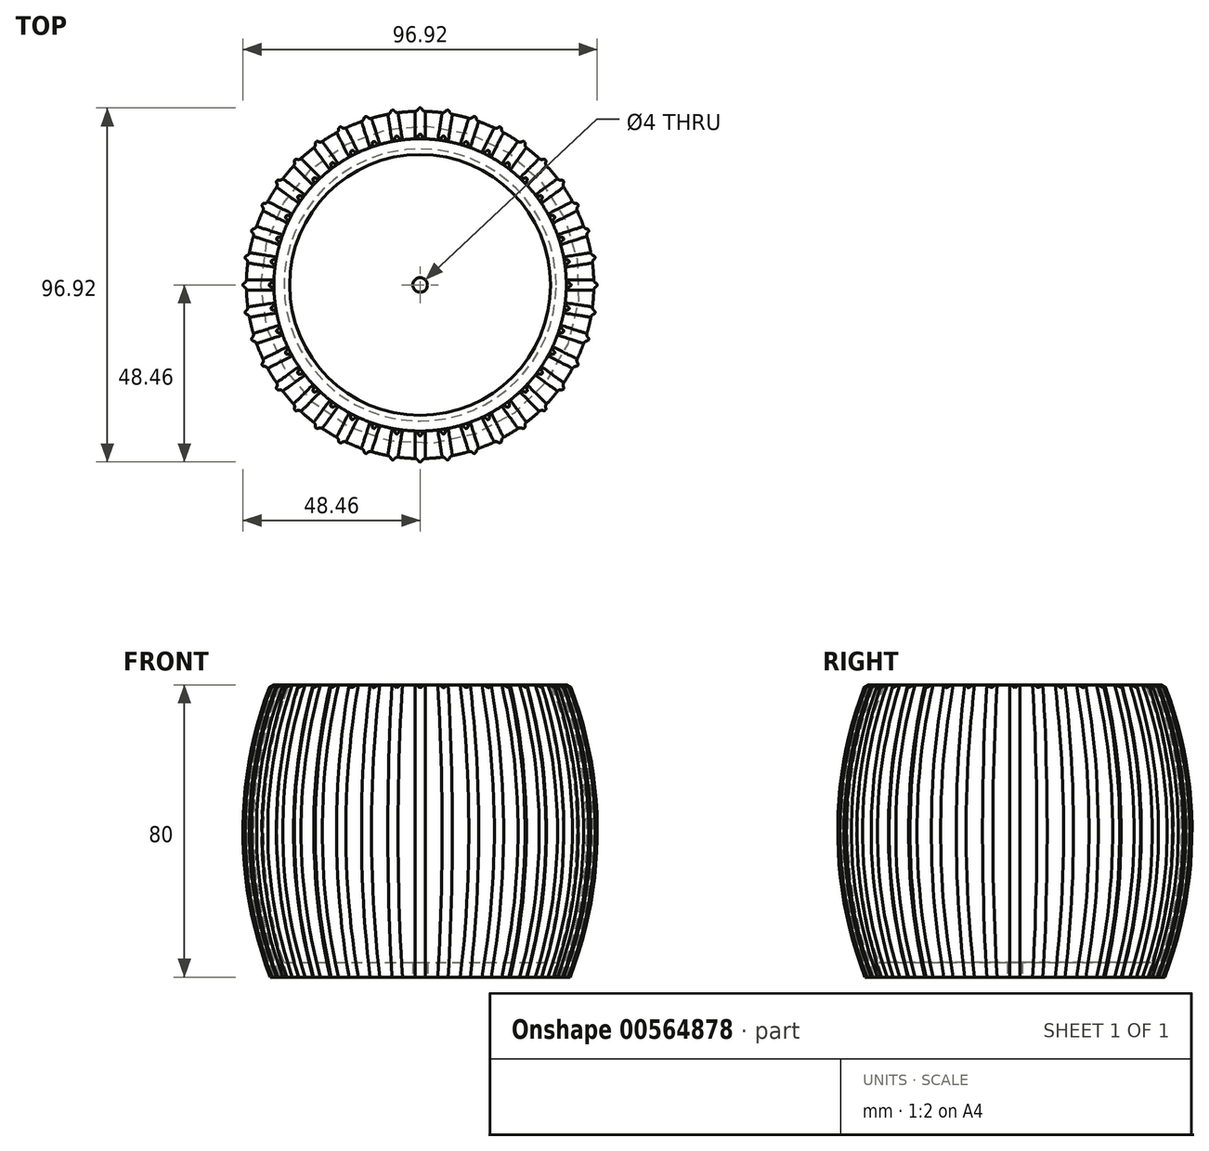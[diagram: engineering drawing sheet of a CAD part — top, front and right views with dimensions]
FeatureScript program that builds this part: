
annotation { "Feature Type Name" : "Feature", "Feature Type Description" : "" }
export const myFeature = defineFeature(function(context is Context, id is Id, definition is map)
    precondition{}
    {
        {
            var Q0;
            Q0=qCreatedBy(makeId("Front.planeOp"),FACE);
            var sketch = newSketch(context, id + "F0", { "sketchPlane" : qUnion([Q0])});
            skLineSegment(sketch, "E0", {"start": v(2, 0) * mm, "end": v(40, 0) * mm});
            skPoint(sketch, "E1", {"position": v(47.53, 40) * mm});
            skArc(sketch, "E2", {"start": v(40, 0) * mm, "mid": v(47.53, 40) * mm, "end": v(40, 80) * mm});
            skArc(sketch, "E3.0", {"start": v(37.23, 4) * mm, "mid": v(43.5, 42.14) * mm, "end": v(35.7, 80) * mm});
            skLineSegment(sketch, "E4", {"start": v(40, 80) * mm, "end": v(35.7, 80) * mm});
            skLineSegment(sketch, "E5", {"start": v(2, 4) * mm, "end": v(37.23, 4) * mm});
            skLineSegment(sketch, "E6", {"start": v(2, 4) * mm, "end": v(2, 0) * mm});
            skLineSegment(sketch, "E7", {"start": v(0, 0) * mm, "end": v(0, 28.98) * mm, "construction": true});
            skSolve(sketch);
        }
        {
            var Q0;
            Q0=makeQuery(id+"F0.imprint","IMPRINT",FACE,{"disambiguationData":[TD([[makeQuery(id+"F0.imprint","IMPRINT",EDGE,{"derivedFrom":sQuery(id+"F0.wireOp",EDGE,"E0")}),1.0]])]});
            var Q1;
            Q1=sQuery(id+"F0.wireOp",EDGE,"E7");
            revolve(context, id + "F1", {"entities" : qUnion([Q0]), "axis" : qUnion([Q1]), "revolveType" : RevolveType.FULL});
        }
        {
            var Q0;
            Q0=qCreatedBy(makeId("Top.planeOp"),FACE);
            var sketch = newSketch(context, id + "F2", { "sketchPlane" : qUnion([Q0])});
            skLineSegment(sketch, "E8", {"start": v(40.47, -0.6) * mm, "end": v(40.75, -0.43) * mm});
            skLineSegment(sketch, "E9", {"start": v(40.75, 0.43) * mm, "end": v(40.47, 0.6) * mm});
            skPoint(sketch, "E10.visualSharp", {"position": v(41.5, 0) * mm});
            skArc(sketch, "E10.filletArc", {"start": v(40.75, -0.43) * mm, "mid": v(41, 0) * mm, "end": v(40.75, 0.43) * mm});
            skPoint(sketch, "E11.center", {"position": v(0, 0) * mm});
            skPoint(sketch, "E12.visualSharp", {"position": v(40, 0.87) * mm});
            skArc(sketch, "E12.filletArc", {"start": v(39.97, 1.42) * mm, "mid": v(40.12, 0.94) * mm, "end": v(40.47, 0.6) * mm});
            skPoint(sketch, "E13.visualSharp", {"position": v(40, -0.87) * mm});
            skArc(sketch, "E13.filletArc", {"start": v(40.47, -0.6) * mm, "mid": v(40.12, -0.94) * mm, "end": v(39.97, -1.42) * mm});
            skArc(sketch, "E14.converted", {"start": v(39.97, 1.42) * mm, "mid": v(40, 0) * mm, "end": v(39.97, -1.42) * mm});
            skSolve(sketch);
        }
        {
            var Q0;
            {var subQ0=sQuery(id+"F2.wireOp",EDGE,"E8");Q0=makeQuery(id+"F2.imprint","IMPRINT",FACE,{"disambiguationData":[TD([[makeQuery(id+"F2.imprint","IMPRINT",EDGE,{"derivedFrom":subQ0}),1.0]])]});}
            var Q1;
            Q1=sQuery(id+"F0.wireOp",EDGE,"E2");
            sweep(context, id + "F3", {"operationType" : NewBodyOperationType.ADD, "profiles" : qUnion([Q0]), "path" : qUnion([Q1])});
        }
        {
            var Q0;
            Q0=makeQuery(id+"F3.opSweep","SWEPT_FACE",FACE,{"disambiguationData":[OSD([sQuery(id+"F0.wireOp",EDGE,"E2"),sQuery(id+"F2.wireOp",EDGE,"E13.filletArc")])]});
            var Q1;
            Q1=makeQuery(id+"F3.opSweep","SWEPT_FACE",FACE,{"disambiguationData":[OSD([sQuery(id+"F0.wireOp",EDGE,"E2"),sQuery(id+"F2.wireOp",EDGE,"E8")])]});
            var Q2;
            Q2=makeQuery(id+"F3.opSweep","SWEPT_FACE",FACE,{"disambiguationData":[OSD([sQuery(id+"F0.wireOp",EDGE,"E2"),sQuery(id+"F2.wireOp",EDGE,"E10.filletArc")])]});
            var Q3;
            Q3=makeQuery(id+"F3.opSweep","SWEPT_FACE",FACE,{"disambiguationData":[OSD([sQuery(id+"F0.wireOp",EDGE,"E2"),sQuery(id+"F2.wireOp",EDGE,"E9")])]});
            var Q4;
            Q4=makeQuery(id+"F3.opSweep","SWEPT_FACE",FACE,{"disambiguationData":[OSD([sQuery(id+"F0.wireOp",EDGE,"E2"),sQuery(id+"F2.wireOp",EDGE,"E12.filletArc")])]});
            var Q5;
            Q5=makeQuery(id+"F3.opSweep","CAP_FACE",FACE,{"disambiguationData":[OSD([sQuery(id+"F0.wireOp",VERTEX,"E2.end"),sQuery(id+"F2.wireOp",EDGE,"E8"),sQuery(id+"F2.wireOp",EDGE,"E9"),sQuery(id+"F2.wireOp",EDGE,"E10.filletArc"),sQuery(id+"F2.wireOp",EDGE,"E12.filletArc"),sQuery(id+"F2.wireOp",EDGE,"E13.filletArc"),sQuery(id+"F2.wireOp",EDGE,"E14.converted")])],"isStart":false});
            var Q6;
            Q6=sQuery(id+"F0.wireOp",EDGE,"E7");
            circularPattern(context, id + "F4", {"patternType" : PatternType.FACE, "faces" : qUnion([Q0, Q1, Q2, Q3, Q4, Q5]), "axis" : qUnion([Q6]), "angle" : 360 * degree, "instanceCount" : 40, "equalSpace" : true});
        }
        {
            var Q0;
            Q0=qCreatedBy(makeId("Front.planeOp"),FACE);
            var sketch = newSketch(context, id + "F5", { "sketchPlane" : qUnion([Q0])});
            skPoint(sketch, "E15.0", {"position": v(40, 80) * mm});
            skLineSegment(sketch, "E16", {"start": v(40, 80) * mm, "end": v(42, 78.85) * mm});
            skLineSegment(sketch, "E17", {"start": v(40, 80) * mm, "end": v(42, 80) * mm, "construction": true});
            skLineSegment(sketch, "E18", {"start": v(42, 81) * mm, "end": v(42, 78.85) * mm});
            skLineSegment(sketch, "E19", {"start": v(40, 80) * mm, "end": v(40, 81) * mm});
            skLineSegment(sketch, "E20", {"start": v(40, 81) * mm, "end": v(42, 81) * mm});
            skSolve(sketch);
        }
        {
            var Q0;
            Q0=makeQuery(id+"F5.imprint","IMPRINT",FACE,{"disambiguationData":[TD([[makeQuery(id+"F5.imprint","IMPRINT",EDGE,{"derivedFrom":sQuery(id+"F5.wireOp",EDGE,"E16")}),1.0]])]});
            var Q1;
            Q1=sQuery(id+"F0.wireOp",EDGE,"E7");
            revolve(context, id + "F6", {"operationType" : NewBodyOperationType.REMOVE, "entities" : qUnion([Q0]), "axis" : qUnion([Q1]), "revolveType" : RevolveType.FULL, "oppositeDirection" : true});
        }
    });
